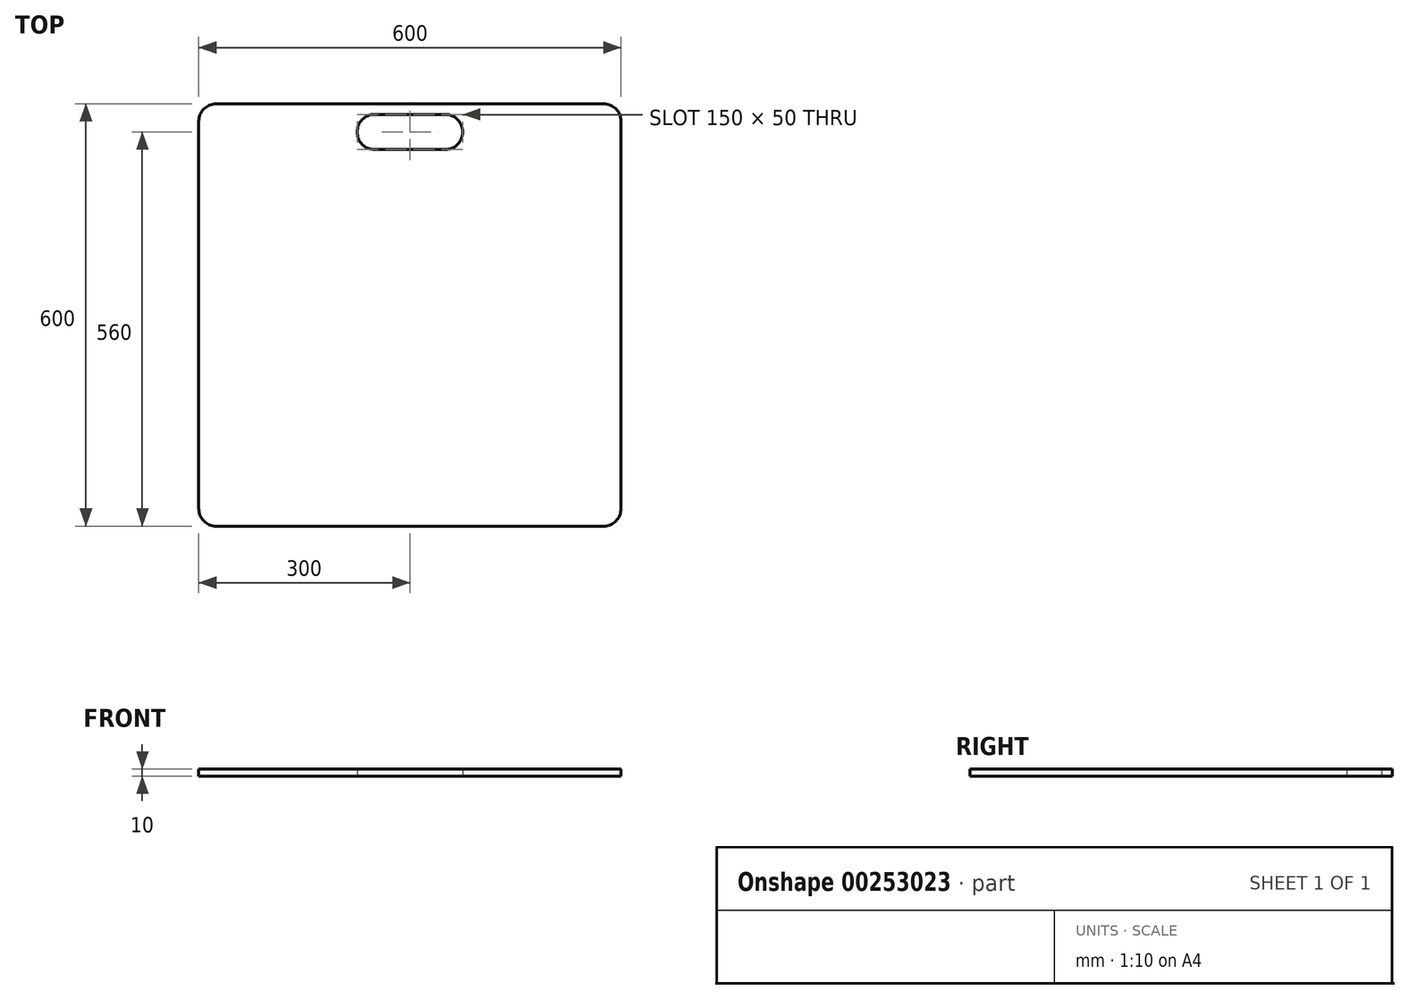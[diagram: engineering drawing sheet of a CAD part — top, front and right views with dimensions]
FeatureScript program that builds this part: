
annotation { "Feature Type Name" : "Feature", "Feature Type Description" : "" }
export const myFeature = defineFeature(function(context is Context, id is Id, definition is map)
    precondition{}
    {
        {
            var Q0;
            Q0=qCreatedBy(makeId("Top.planeOp"),FACE);
            var sketch = newSketch(context, id + "F0", { "sketchPlane" : qUnion([Q0])});
            skLineSegment(sketch, "E0.bottom", {"start": v(-300, 300) * mm, "end": v(300, 300) * mm});
            skLineSegment(sketch, "E0.top", {"start": v(-300, -300) * mm, "end": v(300, -300) * mm});
            skLineSegment(sketch, "E0.left", {"start": v(-300, 300) * mm, "end": v(-300, -300) * mm});
            skLineSegment(sketch, "E0.right", {"start": v(300, 300) * mm, "end": v(300, -300) * mm});
            skPoint(sketch, "E0.middle", {"position": v(0, 0) * mm});
            skSolve(sketch);
        }
        {
            var Q0;
            Q0=qSketchRegion(id+"F0",true);
            extrude(context, id + "F1", {"entities" : qUnion([Q0]), "depth" : 10 * mm});
        }
        {
            var Q0;
            Q0=qCreatedBy(makeId("Top.planeOp"),FACE);
            var sketch = newSketch(context, id + "F2", { "sketchPlane" : qUnion([Q0])});
            skLineSegment(sketch, "E1.bottom", {"start": v(50, 235) * mm, "end": v(-50, 235) * mm});
            skLineSegment(sketch, "E1.top", {"start": v(50, 285) * mm, "end": v(-50, 285) * mm});
            skPoint(sketch, "E1.middle", {"position": v(0, 260) * mm});
            skArc(sketch, "E2", {"start": v(-50, 285) * mm, "mid": v(-75, 260) * mm, "end": v(-50, 235) * mm});
            skArc(sketch, "E3", {"start": v(50, 235) * mm, "mid": v(75, 260) * mm, "end": v(50, 285) * mm});
            skSolve(sketch);
        }
        {
            var Q0;
            Q0=qSketchRegion(id+"F2",true);
            extrude(context, id + "F3", {"entities" : qUnion([Q0]), "operationType" : NewBodyOperationType.REMOVE, "endBound" : BoundingType.THROUGH_ALL, "depth" : 25 * mm});
        }
        {
            var Q0;
            Q0=qCreatedBy(makeId("Front.planeOp"),FACE);
            var sketch = newSketch(context, id + "F4", { "sketchPlane" : qUnion([Q0])});
            skLineSegment(sketch, "E4", {"start": v(0, 0) * mm, "end": v(0, 10) * mm});
            skSolve(sketch);
        }
        {
            var Q0;
            Q0=makeQuery(id+"F1.opExtrude","SWEPT_EDGE",EDGE,{"disambiguationData":[OSD([sQuery(id+"F0.wireOp",EDGE,"E0.top"),sQuery(id+"F0.wireOp",EDGE,"E0.left")])]});
            var Q1;
            Q1=makeQuery(id+"F1.opExtrude","SWEPT_EDGE",EDGE,{"disambiguationData":[OSD([sQuery(id+"F0.wireOp",EDGE,"E0.bottom"),sQuery(id+"F0.wireOp",EDGE,"E0.left")])]});
            var Q2;
            Q2=makeQuery(id+"F1.opExtrude","SWEPT_EDGE",EDGE,{"disambiguationData":[OSD([sQuery(id+"F0.wireOp",EDGE,"E0.bottom"),sQuery(id+"F0.wireOp",EDGE,"E0.right")])]});
            var Q3;
            Q3=makeQuery(id+"F1.opExtrude","SWEPT_EDGE",EDGE,{"disambiguationData":[OSD([sQuery(id+"F0.wireOp",EDGE,"E0.top"),sQuery(id+"F0.wireOp",EDGE,"E0.right")])]});
            fillet(context, id + "F5", {"entities" : qUnion([Q0, Q1, Q2, Q3]), "radius" : 25 * mm, "tangentPropagation" : true, "allowEdgeOverflow" : false});
        }
    });
